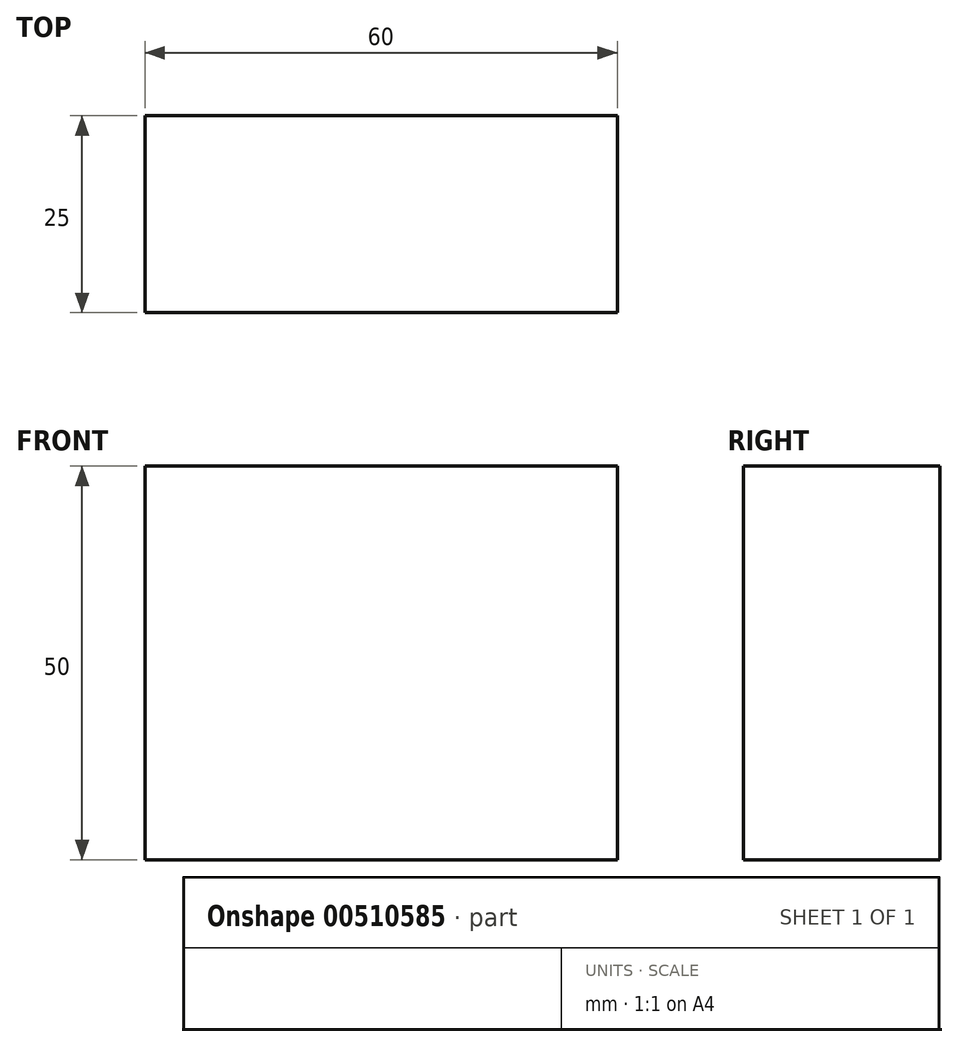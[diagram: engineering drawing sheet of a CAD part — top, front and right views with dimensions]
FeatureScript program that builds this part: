
annotation { "Feature Type Name" : "Feature", "Feature Type Description" : "" }
export const myFeature = defineFeature(function(context is Context, id is Id, definition is map)
    precondition{}
    {
        {
            var Q0;
            Q0=qCreatedBy(makeId("Front.planeOp"),FACE);
            var sketch = newSketch(context, id + "F0", { "sketchPlane" : qUnion([Q0])});
            skLineSegment(sketch, "E0.bottom", {"start": v(0, 0) * mm, "end": v(60, 0) * mm});
            skLineSegment(sketch, "E0.top", {"start": v(0, 50) * mm, "end": v(60, 50) * mm});
            skLineSegment(sketch, "E0.left", {"start": v(0, 0) * mm, "end": v(0, 50) * mm});
            skLineSegment(sketch, "E0.right", {"start": v(60, 0) * mm, "end": v(60, 50) * mm});
            skLineSegment(sketch, "E1.bottom", {"start": v(0, 25) * mm, "end": v(19.41, 25) * mm, "construction": true});
            skLineSegment(sketch, "E1.top", {"start": v(0, 70.3) * mm, "end": v(19.41, 70.3) * mm, "construction": true});
            skLineSegment(sketch, "E1.left", {"start": v(0, 25) * mm, "end": v(0, 70.3) * mm, "construction": true});
            skLineSegment(sketch, "E1.right", {"start": v(19.41, 25) * mm, "end": v(19.41, 70.3) * mm, "construction": true});
            skLineSegment(sketch, "E2.bottom", {"start": v(65.42, 32.67) * mm, "end": v(144.4, 32.67) * mm, "construction": true});
            skLineSegment(sketch, "E2.top", {"start": v(65.42, 0) * mm, "end": v(144.4, 0) * mm, "construction": true});
            skLineSegment(sketch, "E2.left", {"start": v(65.42, 32.67) * mm, "end": v(65.42, 0) * mm, "construction": true});
            skLineSegment(sketch, "E2.right", {"start": v(144.4, 32.67) * mm, "end": v(144.4, 0) * mm, "construction": true});
            skSolve(sketch);
        }
        {
            var Q0;
            Q0 = qSketchRegion(id + "F0", true);
            var sketch = newSketch(context, id + "F1", { "sketchPlane" : qUnion([Q0])});
            skSolve(sketch);
        }
        {
            var Q0;
            Q0=makeQuery(id+"F1.imprint","IMPRINT",FACE,{"disambiguationData":[TD([[makeQuery(id+"F1.imprint","IMPRINT",EDGE,{"derivedFrom":makeQuery(id+"F0.imprint","IMPRINT",EDGE,{"derivedFrom":sQuery(id+"F0.wireOp",EDGE,"E0.bottom")})}),1.0]])]});
            extrude(context, id + "F2", {"entities" : qUnion([Q0]), "depth" : 25 * mm});
        }
    });
